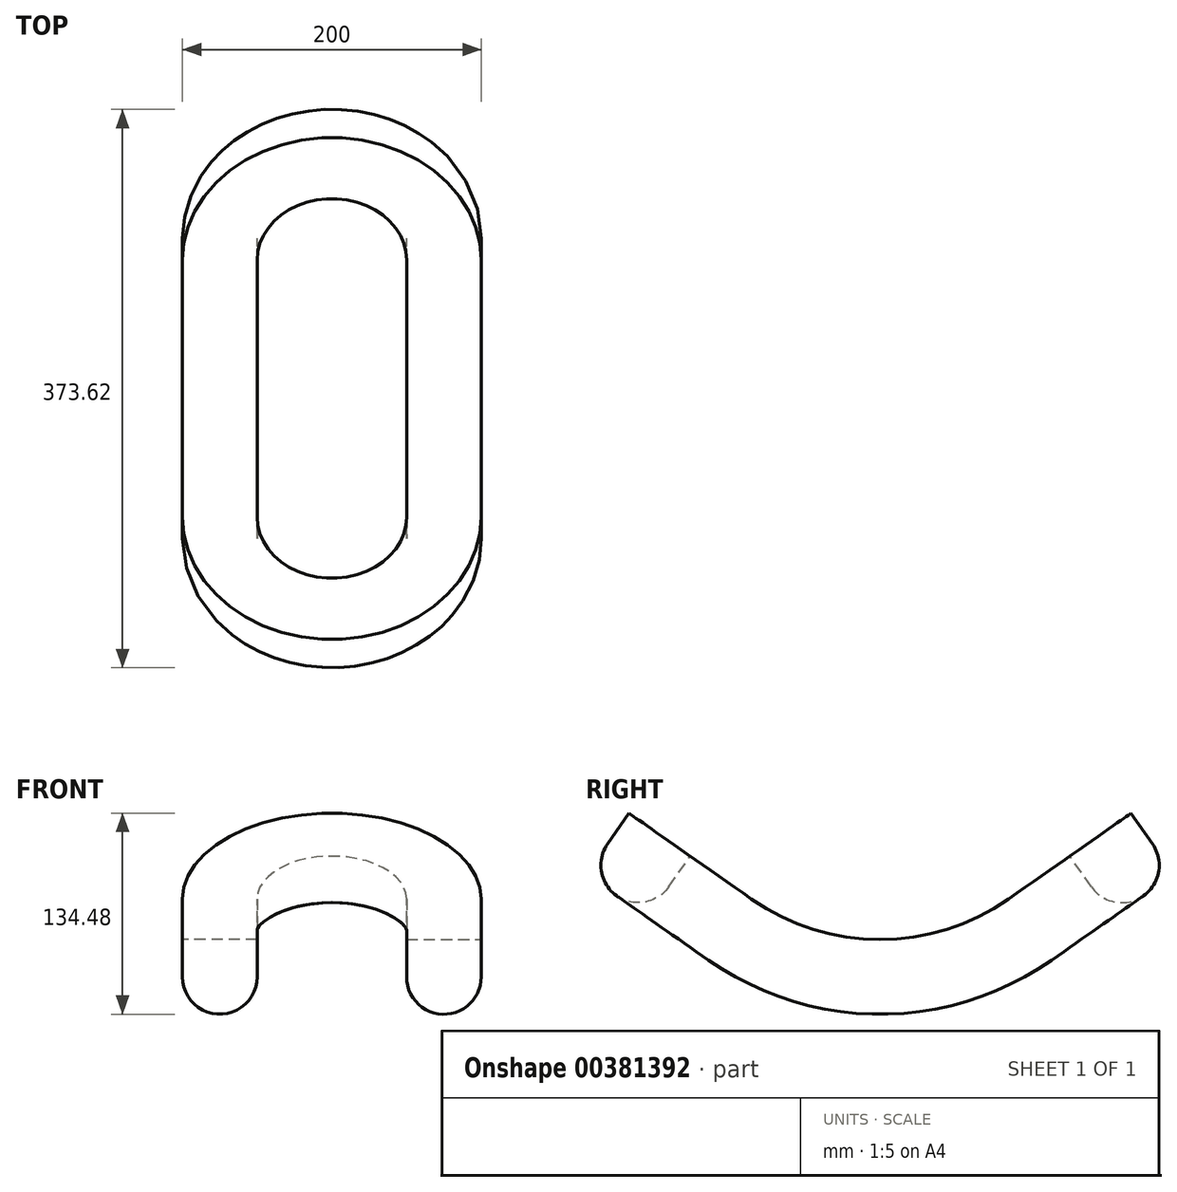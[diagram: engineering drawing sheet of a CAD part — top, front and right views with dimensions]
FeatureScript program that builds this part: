
annotation { "Feature Type Name" : "Feature", "Feature Type Description" : "" }
export const myFeature = defineFeature(function(context is Context, id is Id, definition is map)
    precondition{}
    {
        {
            var Q0;
            Q0=qCreatedBy(makeId("Right.planeOp"),FACE);
            var sketch = newSketch(context, id + "F0", { "sketchPlane" : qUnion([Q0])});
            skArc(sketch, "E0", {"start": v(0, 0) * mm, "mid": v(45.1, 6.94) * mm, "end": v(86.04, 27.13) * mm});
            skLineSegment(sketch, "E1", {"start": v(86.04, 27.13) * mm, "end": v(167.95, 84.48) * mm});
            skLineSegment(sketch, "E2", {"start": v(86.04, 27.13) * mm, "end": v(0, 150) * mm, "construction": true});
            skSolve(sketch);
        }
        {
            var Q0;
            Q0 = qConstructionFilter(qBodyType(qCreatedBy(id + "F0" ,EDGE), BodyType.WIRE), ConstructionObject.NO);
            extrude(context, id + "F1", {"bodyType" : ToolBodyType.SURFACE, "surfaceEntities" : qUnion([Q0]), "depth" : 100 * mm});
        }
        {
            var Q0;
            Q0=makeQuery(id+"F1.opExtrude","SWEPT_FACE",FACE,{"disambiguationData":[OSD([sQuery(id+"F0.wireOp",EDGE,"E1")])]});
            var sketch = newSketch(context, id + "F2", { "sketchPlane" : qUnion([Q0])});
            skArc(sketch, "E3", {"start": v(0, -186.04) * mm, "mid": v(70.71, -156.75) * mm, "end": v(100, -86.04) * mm});
            skSolve(sketch);
        }
        {
            var Q0;
            Q0=qCreatedBy(makeId("Front.planeOp"),FACE);
            var sketch = newSketch(context, id + "F3", { "sketchPlane" : qUnion([Q0])});
            skLineSegment(sketch, "E4", {"start": v(50, 0) * mm, "end": v(100, 0) * mm});
            skLineSegment(sketch, "E5", {"start": v(100, 0) * mm, "end": v(100, -25) * mm});
            skLineSegment(sketch, "E6", {"start": v(50, 0) * mm, "end": v(50, -25) * mm});
            skArc(sketch, "E7", {"start": v(50, -25) * mm, "mid": v(75, -50) * mm, "end": v(100, -25) * mm});
            skSolve(sketch);
        }
        {
            var Q0;
            Q0 = qSketchRegion(id + "F3", true);
            var Q1;
            Q1=makeQuery(id+"F1.opExtrude","CAP_EDGE",EDGE,{"disambiguationData":[OSD([sQuery(id+"F0.wireOp",EDGE,"E0")])],"isStart":false});
            var Q2;
            Q2=sQuery(id+"F2.wireOp",EDGE,"E3");
            sweep(context, id + "F4", {"profiles" : qUnion([Q0]), "path" : qUnion([Q1, Q2])});
        }
        {
            var Q0;
            Q0=makeQuery(id+"F4.opSweep","SWEPT_BODY",BODY,{"disambiguationData":[OSD([sQuery(id+"F2.wireOp",EDGE,"E3"),sQuery(id+"F3.wireOp",EDGE,"E4"),sQuery(id+"F3.wireOp",EDGE,"E5"),sQuery(id+"F3.wireOp",EDGE,"E6"),sQuery(id+"F3.wireOp",EDGE,"E7")])]});
            var Q1;
            Q1=qCreatedBy(makeId("Right.planeOp"),FACE);
            mirror(context, id + "F5", {"operationType" : NewBodyOperationType.ADD, "entities" : qUnion([Q0]), "mirrorPlane" : qUnion([Q1])});
        }
        {
            var Q0;
            Q0=makeQuery(id+"F4.opSweep","SWEPT_BODY",BODY,{"disambiguationData":[OSD([sQuery(id+"F2.wireOp",EDGE,"E3"),sQuery(id+"F3.wireOp",EDGE,"E4"),sQuery(id+"F3.wireOp",EDGE,"E5"),sQuery(id+"F3.wireOp",EDGE,"E6"),sQuery(id+"F3.wireOp",EDGE,"E7")])]});
            var Q1;
            Q1=qCreatedBy(makeId("Front.planeOp"),FACE);
            mirror(context, id + "F6", {"operationType" : NewBodyOperationType.ADD, "entities" : qUnion([Q0]), "mirrorPlane" : qUnion([Q1])});
        }
    });
